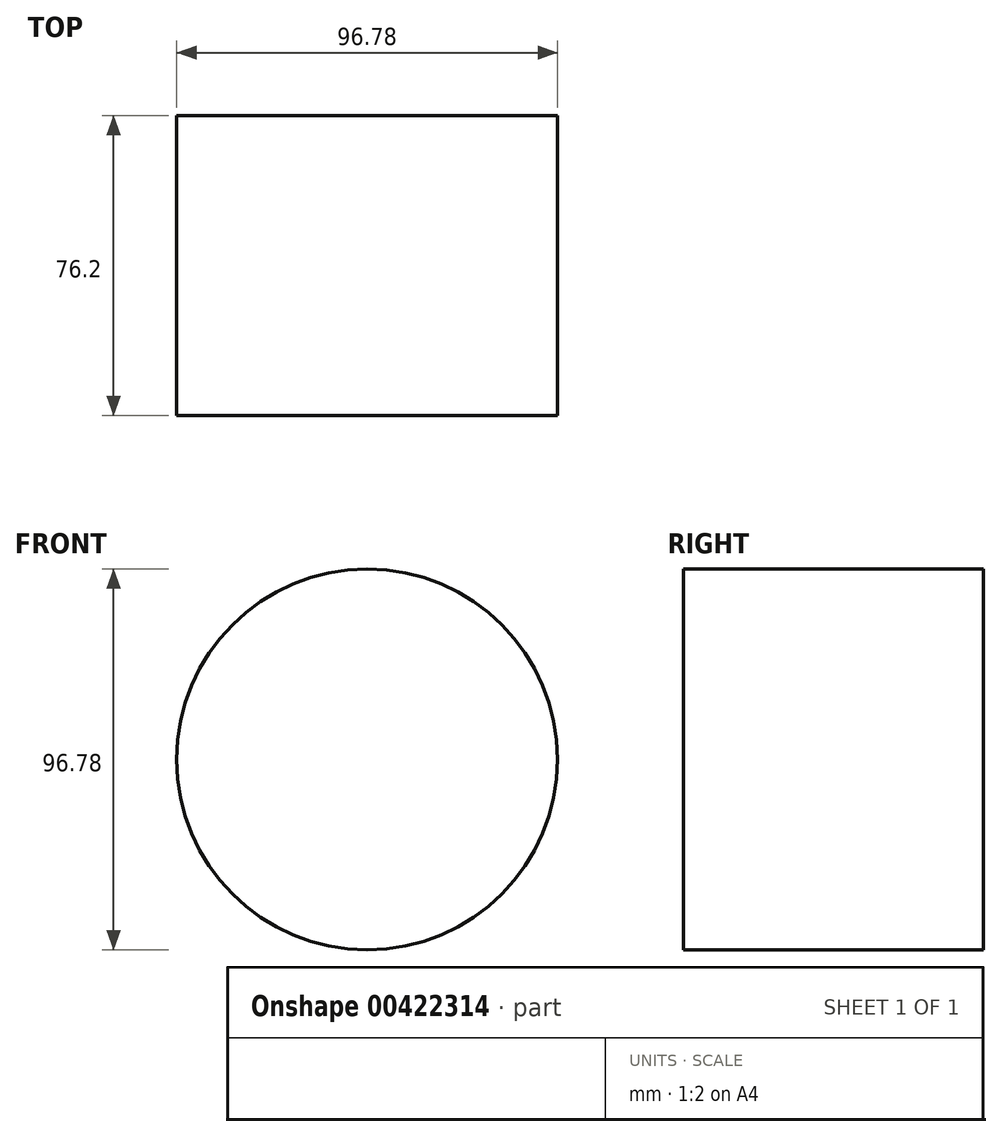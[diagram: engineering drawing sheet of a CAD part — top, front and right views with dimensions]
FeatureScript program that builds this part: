
annotation { "Feature Type Name" : "Feature", "Feature Type Description" : "" }
export const myFeature = defineFeature(function(context is Context, id is Id, definition is map)
    precondition{}
    {
        {
            var Q0;
            Q0=qCreatedBy(makeId("Front.planeOp"),FACE);
            var sketch = newSketch(context, id + "F0", { "sketchPlane" : qUnion([Q0])});
            skCircle(sketch, "E0", {"center": v(1.54, 0) * mm, "radius": 48.4 * mm});
            skSolve(sketch);
        }
        {
            var Q0;
            Q0=makeQuery(id+"F0.imprint","IMPRINT",FACE,{"disambiguationData":[TD([[makeQuery(id+"F0.imprint","IMPRINT",EDGE,{"derivedFrom":sQuery(id+"F0.wireOp",EDGE,"E0")}),1.0]])]});
            extrude(context, id + "F1", {"entities" : qUnion([Q0]), "depth" : 76.2 * mm});
        }
    });
